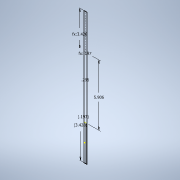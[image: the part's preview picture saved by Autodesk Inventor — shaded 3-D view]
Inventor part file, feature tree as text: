
AUTODESK INVENTOR PART (.ipt)
format: ipt  version: 2020 (Build 240168000, 168)  size: 103,424 bytes
history: native  units: in
note: dims shown in document units (in); Inventor stores cm internally (conversion verified against a paired STEP export)
features: other x2, extrude x1, sketch x1, reference x1
ambient origin geometry x8: Origin, YZ Plane, XZ Plane, XY Plane, X Axis, Y Axis, Z Axis, Center Point
bodies: Solid1 (feature_tree)
feature tree (5):
  extrude  "Extrusion1"  Depth=0.75in
  sketch  "Sketch1"  dims[d0=0.1969in d1=0.1969in d2=3.4282in d3=3.4282in d4=5.9055in d5=0.2953in d6=0.75in d7=0.0in]
  reference  "Reference1"
  other  "Assembly1"
  other  "Holder:2"
